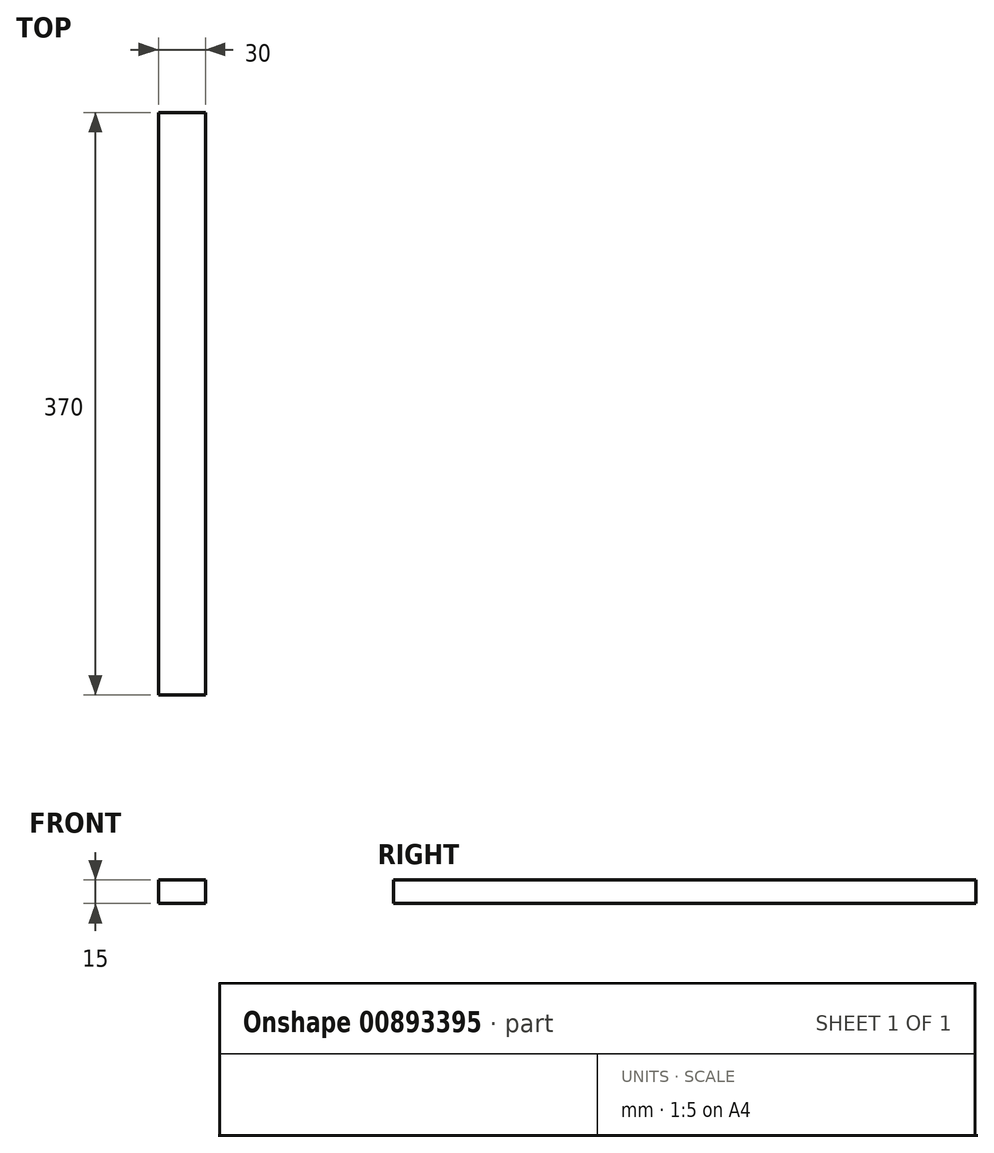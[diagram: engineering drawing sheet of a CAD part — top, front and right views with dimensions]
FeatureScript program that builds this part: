
annotation { "Feature Type Name" : "Feature", "Feature Type Description" : "" }
export const myFeature = defineFeature(function(context is Context, id is Id, definition is map)
    precondition{}
    {
        {
            var Q0;
            Q0=qCreatedBy(makeId("Front.planeOp"),FACE);
            var sketch = newSketch(context, id + "F0", { "sketchPlane" : qUnion([Q0])});
            skLineSegment(sketch, "E0.bottom", {"start": v(0, 0) * mm, "end": v(30, 0) * mm});
            skLineSegment(sketch, "E0.top", {"start": v(0, 15) * mm, "end": v(30, 15) * mm});
            skLineSegment(sketch, "E0.left", {"start": v(0, 0) * mm, "end": v(0, 15) * mm});
            skLineSegment(sketch, "E0.right", {"start": v(30, 0) * mm, "end": v(30, 15) * mm});
            skSolve(sketch);
        }
        {
            var Q0;
            Q0=makeQuery(id+"F0.imprint","IMPRINT",FACE,{"disambiguationData":[TD([[makeQuery(id+"F0.imprint","IMPRINT",EDGE,{"derivedFrom":sQuery(id+"F0.wireOp",EDGE,"E0.bottom")}),1.0]])]});
            extrude(context, id + "F1", {"entities" : qUnion([Q0]), "depth" : 370 * mm, "offsetDistance" : 25.4 * mm});
        }
    });
